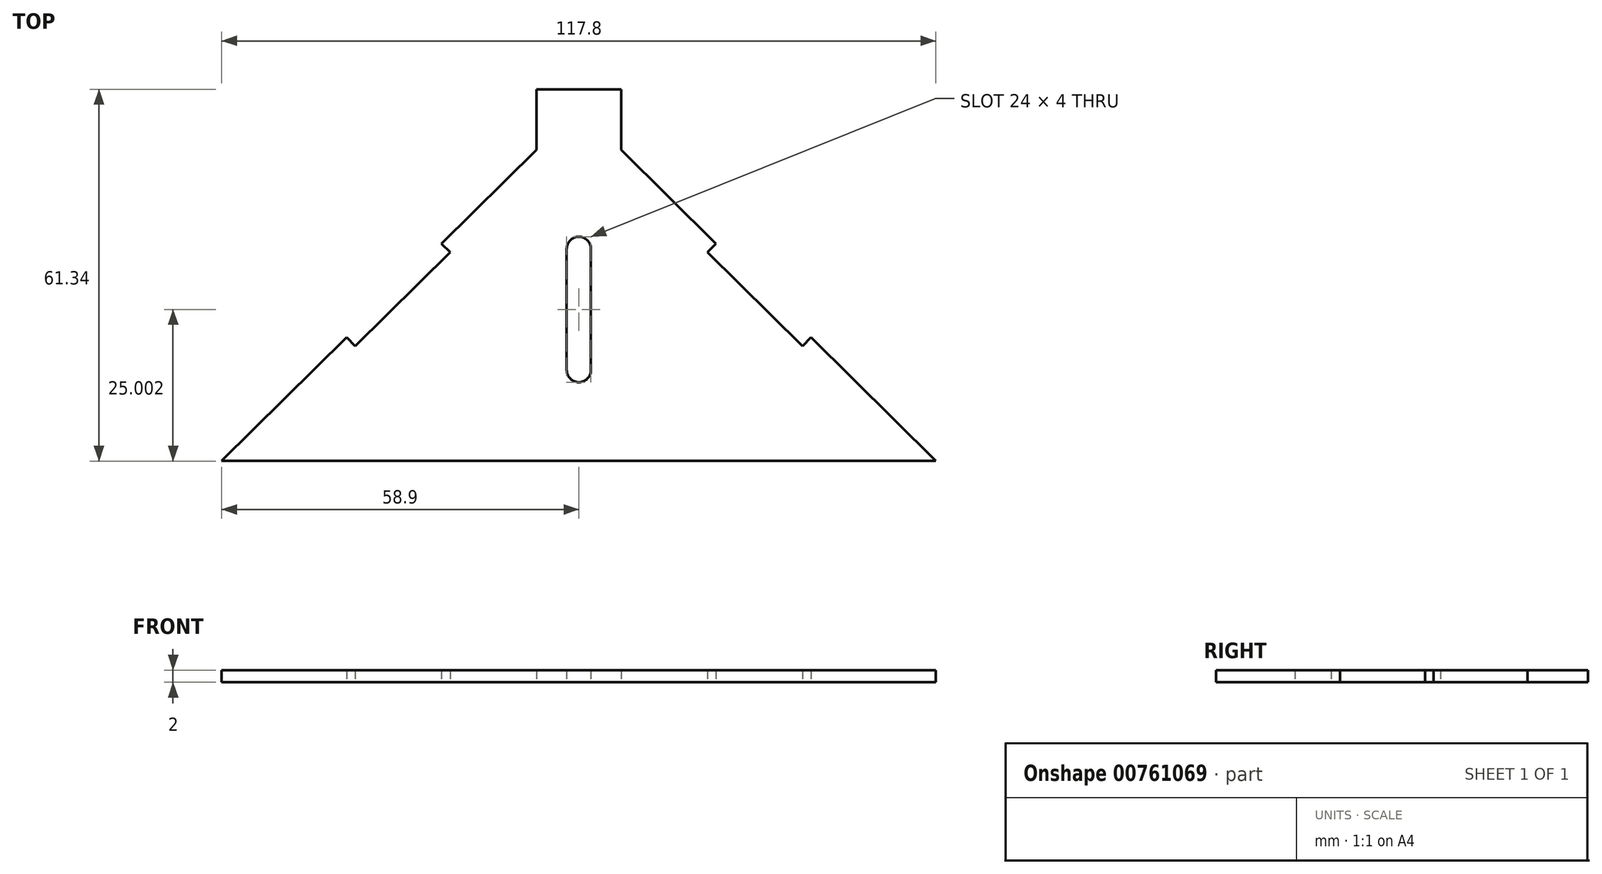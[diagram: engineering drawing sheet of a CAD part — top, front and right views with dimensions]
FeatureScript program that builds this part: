
annotation { "Feature Type Name" : "Feature", "Feature Type Description" : "" }
export const myFeature = defineFeature(function(context is Context, id is Id, definition is map)
    precondition{}
    {
        {
            var Q0;
            Q0=qCreatedBy(makeId("Top.planeOp"),FACE);
            var sketch = newSketch(context, id + "F0", { "sketchPlane" : qUnion([Q0])});
            skLineSegment(sketch, "E0", {"start": v(-23.23, 26.47) * mm, "end": v(-24.64, 27.89) * mm});
            skLineSegment(sketch, "E1", {"start": v(-9, 43.36) * mm, "end": v(-9, 53.36) * mm});
            skLineSegment(sketch, "E2", {"start": v(-9, 53.36) * mm, "end": v(5, 53.36) * mm});
            skLineSegment(sketch, "E3", {"start": v(5, 53.36) * mm, "end": v(5, 43.36) * mm});
            skLineSegment(sketch, "E4", {"start": v(-23.23, 26.47) * mm, "end": v(-38.87, 11) * mm});
            skLineSegment(sketch, "E5", {"start": v(-38.87, 11) * mm, "end": v(-40.28, 12.42) * mm});
            skLineSegment(sketch, "E6", {"start": v(-9, 43.36) * mm, "end": v(-24.64, 27.89) * mm});
            skLineSegment(sketch, "E7", {"start": v(-40.28, 12.42) * mm, "end": v(-60.9, -7.98) * mm});
            skLineSegment(sketch, "E8", {"start": v(19.23, 26.47) * mm, "end": v(20.64, 27.89) * mm});
            skLineSegment(sketch, "E9", {"start": v(20.64, 27.89) * mm, "end": v(19.23, 26.47) * mm});
            skLineSegment(sketch, "E10", {"start": v(19.23, 26.47) * mm, "end": v(34.87, 11) * mm});
            skLineSegment(sketch, "E11", {"start": v(34.87, 11) * mm, "end": v(36.28, 12.42) * mm});
            skLineSegment(sketch, "E12", {"start": v(5, 43.36) * mm, "end": v(20.64, 27.89) * mm});
            skLineSegment(sketch, "E13", {"start": v(36.28, 12.42) * mm, "end": v(56.9, -7.98) * mm});
            skLineSegment(sketch, "E14", {"start": v(-60.9, -7.98) * mm, "end": v(56.9, -7.98) * mm});
            skLineSegment(sketch, "E15", {"start": v(0, 7.02) * mm, "end": v(0, 27.02) * mm});
            skLineSegment(sketch, "E16", {"start": v(-4, 27.02) * mm, "end": v(-4, 7.02) * mm});
            skArc(sketch, "E17", {"start": v(0, 27.02) * mm, "mid": v(-2, 29.02) * mm, "end": v(-4, 27.02) * mm});
            skArc(sketch, "E18", {"start": v(-4, 7.02) * mm, "mid": v(-2, 5.02) * mm, "end": v(0, 7.02) * mm});
            skSolve(sketch);
        }
        {
            var Q0;
            Q0=qSketchRegion(id+"F0",true);
            extrude(context, id + "F1", {"entities" : qUnion([Q0]), "depth" : 2 * mm, "offsetDistance" : 25 * mm});
        }
    });
